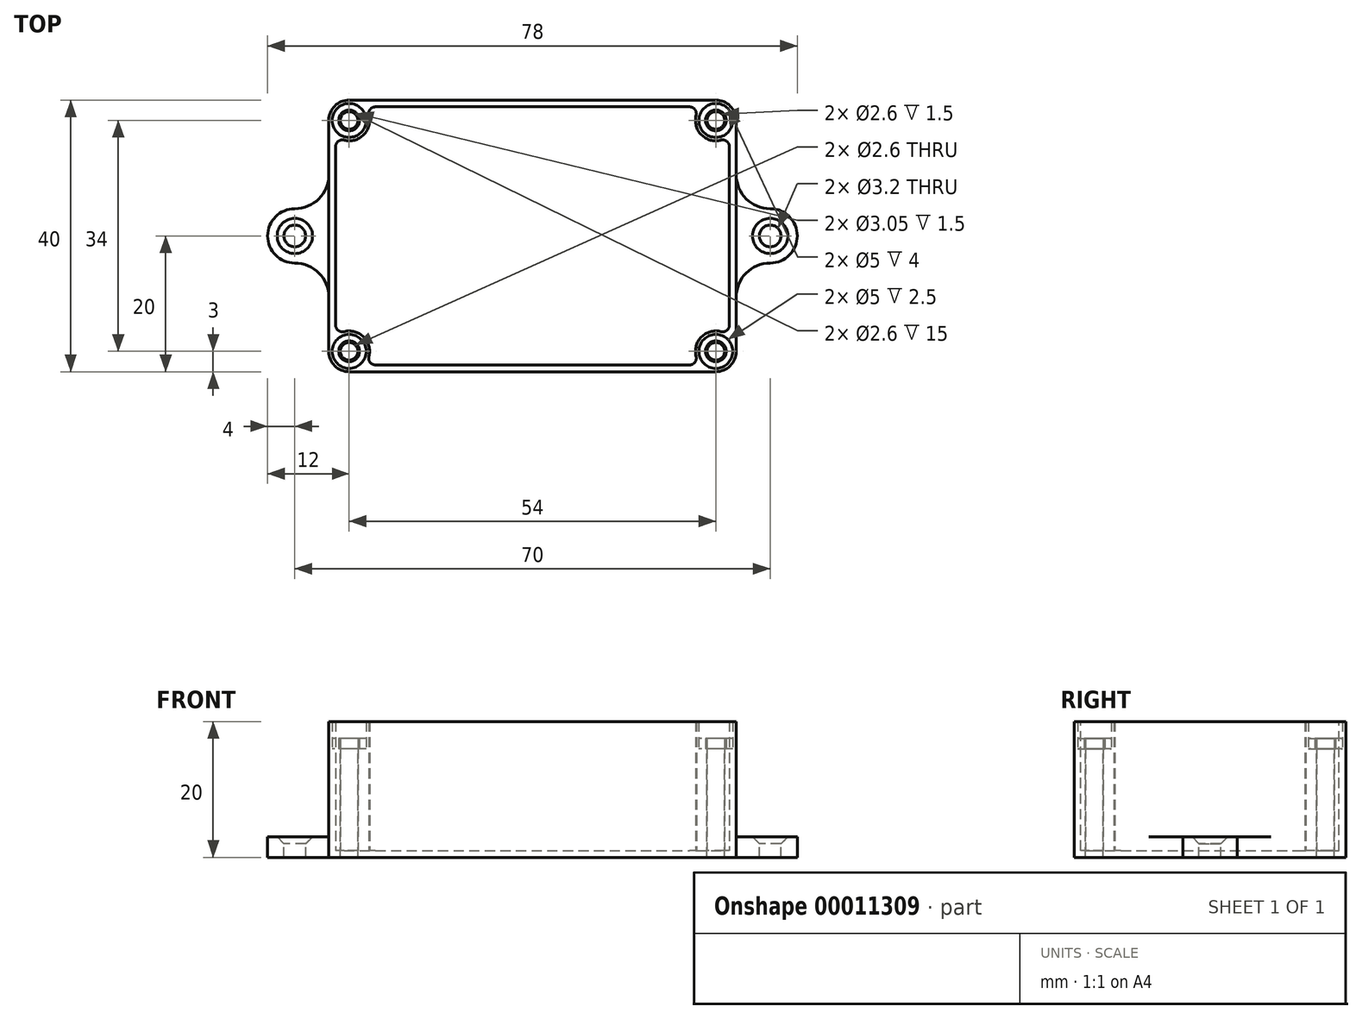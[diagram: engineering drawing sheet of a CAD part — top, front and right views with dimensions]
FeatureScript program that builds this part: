
annotation { "Feature Type Name" : "Feature", "Feature Type Description" : "" }
export const myFeature = defineFeature(function(context is Context, id is Id, definition is map)
    precondition{}
    {
        {
            var Q0;
            Q0=qCreatedBy(makeId("Top.planeOp"),FACE);
            var sketch = newSketch(context, id + "F0", { "sketchPlane" : qUnion([Q0])});
            skLineSegment(sketch, "E0.bottom", {"start": v(-27, 20) * mm, "end": v(27, 20) * mm});
            skLineSegment(sketch, "E0.top", {"start": v(-27, -20) * mm, "end": v(27, -20) * mm});
            skLineSegment(sketch, "E0.left", {"start": v(-30, 17) * mm, "end": v(-30, -17) * mm});
            skLineSegment(sketch, "E0.right", {"start": v(30, 17) * mm, "end": v(30, -17) * mm});
            skLineSegment(sketch, "E1", {"start": v(0, 0) * mm, "end": v(0, 30.82) * mm, "construction": true});
            skLineSegment(sketch, "E2", {"start": v(0, 0) * mm, "end": v(-60.1, 0) * mm, "construction": true});
            skArc(sketch, "E3", {"start": v(-27, 20) * mm, "mid": v(-29.12, 19.12) * mm, "end": v(-30, 17) * mm});
            skLineSegment(sketch, "E4", {"start": v(-30, -4) * mm, "end": v(-35, -4) * mm});
            skLineSegment(sketch, "E5", {"start": v(-30, 4) * mm, "end": v(-35, 4) * mm});
            skArc(sketch, "E6", {"start": v(-35, 4) * mm, "mid": v(-39, 0) * mm, "end": v(-35, -4) * mm});
            skCircle(sketch, "E7", {"center": v(-35, 0) * mm, "radius": 1.6 * mm});
            skLineSegment(sketch, "E8.0.MirrorCS", {"start": v(30, 4) * mm, "end": v(35, 4) * mm});
            skArc(sketch, "E9.0.MirrorCS", {"start": v(35, 4) * mm, "mid": v(39, 0) * mm, "end": v(35, -4) * mm});
            skCircle(sketch, "E10.0.MirrorC", {"center": v(35, 0) * mm, "radius": 1.6 * mm});
            skLineSegment(sketch, "E11.0.MirrorCS", {"start": v(30, -4) * mm, "end": v(35, -4) * mm});
            skCircle(sketch, "E12", {"center": v(-27, 17) * mm, "radius": 1.3 * mm});
            skLineSegment(sketch, "E13", {"start": v(-24.76, 19) * mm, "end": v(0, 19) * mm});
            skLineSegment(sketch, "E14", {"start": v(-29, 0) * mm, "end": v(-29, 14.76) * mm});
            skArc(sketch, "E15.trimOffspring", {"start": v(-29, 14.76) * mm, "mid": v(-24.88, 14.88) * mm, "end": v(-24.76, 19) * mm});
            skLineSegment(sketch, "E16.0.MirrorCS", {"start": v(24.76, 19) * mm, "end": v(0, 19) * mm});
            skArc(sketch, "E17.0.MirrorCS", {"start": v(29, 14.76) * mm, "mid": v(24.88, 14.88) * mm, "end": v(24.76, 19) * mm});
            skLineSegment(sketch, "E18.0.MirrorCS", {"start": v(29, 0) * mm, "end": v(29, 14.76) * mm});
            skCircle(sketch, "E19.0.MirrorC", {"center": v(27, 17) * mm, "radius": 1.3 * mm});
            skArc(sketch, "E20.0.MirrorCS", {"start": v(27, 20) * mm, "mid": v(29.12, 19.12) * mm, "end": v(30, 17) * mm});
            skLineSegment(sketch, "E21.0.MirrorCS", {"start": v(-29, 0) * mm, "end": v(-29, -14.76) * mm});
            skArc(sketch, "E22.0.MirrorCS", {"start": v(-29, -14.76) * mm, "mid": v(-24.88, -14.88) * mm, "end": v(-24.76, -19) * mm});
            skCircle(sketch, "E23.0.MirrorC", {"center": v(-27, -17) * mm, "radius": 1.3 * mm});
            skArc(sketch, "E24.0.MirrorCS", {"start": v(-27, -20) * mm, "mid": v(-29.12, -19.12) * mm, "end": v(-30, -17) * mm});
            skLineSegment(sketch, "E25.0.MirrorCS", {"start": v(-24.76, -19) * mm, "end": v(0, -19) * mm});
            skArc(sketch, "E26.0.MirrorCS", {"start": v(29, -14.76) * mm, "mid": v(24.88, -14.88) * mm, "end": v(24.76, -19) * mm});
            skCircle(sketch, "E27.0.MirrorC", {"center": v(27, -17) * mm, "radius": 1.3 * mm});
            skLineSegment(sketch, "E28.0.MirrorCS", {"start": v(24.76, -19) * mm, "end": v(0, -19) * mm});
            skLineSegment(sketch, "E29.0.MirrorCS", {"start": v(29, 0) * mm, "end": v(29, -14.76) * mm});
            skArc(sketch, "E30.0.MirrorCS", {"start": v(27, -20) * mm, "mid": v(29.12, -19.12) * mm, "end": v(30, -17) * mm});
            skSolve(sketch);
        }
        {
            var Q0;
            {var subQ1=sQuery(id+"F0.wireOp",EDGE,"E4");Q0=makeQuery(id+"F0.imprint","IMPRINT",FACE,{"disambiguationData":[TD([[makeQuery(id+"F0.imprint","IMPRINT",EDGE,{"derivedFrom":subQ1}),-1.0]])]});}
            var Q1;
            Q1=makeQuery(id+"F0.imprint","IMPRINT",FACE,{"disambiguationData":[TD([[makeQuery(id+"F0.imprint","IMPRINT",EDGE,{"derivedFrom":sQuery(id+"F0.wireOp",EDGE,"E0.bottom")}),-1.0]])]});
            var Q2;
            Q2=makeQuery(id+"F0.imprint","IMPRINT",FACE,{"disambiguationData":[TD([[makeQuery(id+"F0.imprint","IMPRINT",EDGE,{"derivedFrom":sQuery(id+"F0.wireOp",EDGE,"E12")}),1.0]])]});
            var Q3;
            Q3=makeQuery(id+"F0.imprint","IMPRINT",FACE,{"disambiguationData":[TD([[makeQuery(id+"F0.imprint","IMPRINT",EDGE,{"derivedFrom":sQuery(id+"F0.wireOp",EDGE,"E23.0.MirrorC")}),-1.0]])]});
            var Q4;
            Q4=makeQuery(id+"F0.imprint","IMPRINT",FACE,{"disambiguationData":[TD([[makeQuery(id+"F0.imprint","IMPRINT",EDGE,{"derivedFrom":sQuery(id+"F0.wireOp",EDGE,"E13")}),-1.0]])]});
            var Q5;
            Q5=makeQuery(id+"F0.imprint","IMPRINT",FACE,{"disambiguationData":[TD([[makeQuery(id+"F0.imprint","IMPRINT",EDGE,{"derivedFrom":sQuery(id+"F0.wireOp",EDGE,"E19.0.MirrorC")}),-1.0]])]});
            var Q6;
            Q6=makeQuery(id+"F0.imprint","IMPRINT",FACE,{"disambiguationData":[TD([[makeQuery(id+"F0.imprint","IMPRINT",EDGE,{"derivedFrom":sQuery(id+"F0.wireOp",EDGE,"E27.0.MirrorC")}),1.0]])]});
            var Q7;
            {var subQ1=sQuery(id+"F0.wireOp",EDGE,"E8.0.MirrorCS");Q7=makeQuery(id+"F0.imprint","IMPRINT",FACE,{"disambiguationData":[TD([[makeQuery(id+"F0.imprint","IMPRINT",EDGE,{"derivedFrom":subQ1}),-1.0]])]});}
            extrude(context, id + "F1", {"entities" : qUnion([Q0, Q1, Q2, Q3, Q4, Q5, Q6, Q7]), "oppositeDirection" : true, "depth" : 1 * mm});
        }
        {
            var Q0;
            Q0=makeQuery(id+"F1.opExtrude","SWEPT_EDGE",EDGE,{"disambiguationData":[OSD([sQuery(id+"F0.wireOp",EDGE,"E0.left"),sQuery(id+"F0.wireOp",EDGE,"E5")])]});
            var Q1;
            Q1=makeQuery(id+"F1.opExtrude","SWEPT_EDGE",EDGE,{"disambiguationData":[OSD([sQuery(id+"F0.wireOp",EDGE,"E0.left"),sQuery(id+"F0.wireOp",EDGE,"E4")])]});
            var Q2;
            Q2=makeQuery(id+"F1.opExtrude","SWEPT_EDGE",EDGE,{"disambiguationData":[OSD([sQuery(id+"F0.wireOp",EDGE,"E0.right"),sQuery(id+"F0.wireOp",EDGE,"E11.0.MirrorCS")])]});
            var Q3;
            Q3=makeQuery(id+"F1.opExtrude","SWEPT_EDGE",EDGE,{"disambiguationData":[OSD([sQuery(id+"F0.wireOp",EDGE,"E0.right"),sQuery(id+"F0.wireOp",EDGE,"E8.0.MirrorCS")])]});
            fillet(context, id + "F2", {"entities" : qUnion([Q0, Q1, Q2, Q3]), "radius" : 5 * mm, "tangentPropagation" : true, "allowEdgeOverflow" : false});
        }
        {
            var Q0;
            Q0=makeQuery(id+"F0.imprint","IMPRINT",FACE,{"disambiguationData":[TD([[makeQuery(id+"F0.imprint","IMPRINT",EDGE,{"derivedFrom":sQuery(id+"F0.wireOp",EDGE,"E0.bottom")}),-1.0]])]});
            extrude(context, id + "F3", {"entities" : qUnion([Q0]), "operationType" : NewBodyOperationType.ADD, "depth" : 15 * mm});
        }
        {
            var Q0;
            {var subQ0=sQuery(id+"F0.wireOp",EDGE,"E0.left");var subQ1=sQuery(id+"F0.wireOp",EDGE,"E3");var subQ2=sQuery(id+"F0.wireOp",EDGE,"E4");var subQ3=sQuery(id+"F0.wireOp",EDGE,"E5");var subQ4=sQuery(id+"F0.wireOp",EDGE,"E6");var subQ5=sQuery(id+"F0.wireOp",EDGE,"E7");var subQ6=sQuery(id+"F0.wireOp",EDGE,"E24.0.MirrorCS");Q0=makeQuery(id+"F3.boolean.opBoolean","SPLIT",FACE,{"disambiguationData":[TD([makeQuery(id+"F1.opExtrude","SWEPT_FACE",FACE,{"disambiguationData":[OSD([subQ4])]})])],"derivedFrom":makeQuery(id+"F1.opExtrude","CAP_FACE",FACE,{"disambiguationData":[OSD([sQuery(id+"F0.wireOp",EDGE,"E0.bottom"),sQuery(id+"F0.wireOp",EDGE,"E0.top"),subQ0,sQuery(id+"F0.wireOp",EDGE,"E0.right"),subQ1,subQ2,subQ3,subQ4,subQ5,sQuery(id+"F0.wireOp",EDGE,"E8.0.MirrorCS"),sQuery(id+"F0.wireOp",EDGE,"E9.0.MirrorCS"),sQuery(id+"F0.wireOp",EDGE,"E10.0.MirrorC"),sQuery(id+"F0.wireOp",EDGE,"E11.0.MirrorCS"),sQuery(id+"F0.wireOp",EDGE,"E20.0.MirrorCS"),subQ6,sQuery(id+"F0.wireOp",EDGE,"E30.0.MirrorCS")])],"isStart":true})});}
            var Q1;
            {var subQ0=sQuery(id+"F0.wireOp",EDGE,"E0.right");var subQ1=sQuery(id+"F0.wireOp",EDGE,"E8.0.MirrorCS");var subQ2=sQuery(id+"F0.wireOp",EDGE,"E9.0.MirrorCS");var subQ3=sQuery(id+"F0.wireOp",EDGE,"E10.0.MirrorC");var subQ4=sQuery(id+"F0.wireOp",EDGE,"E11.0.MirrorCS");var subQ5=sQuery(id+"F0.wireOp",EDGE,"E20.0.MirrorCS");var subQ6=sQuery(id+"F0.wireOp",EDGE,"E30.0.MirrorCS");Q1=makeQuery(id+"F3.boolean.opBoolean","SPLIT",FACE,{"disambiguationData":[TD([makeQuery(id+"F1.opExtrude","SWEPT_FACE",FACE,{"disambiguationData":[OSD([subQ2])]})])],"derivedFrom":makeQuery(id+"F1.opExtrude","CAP_FACE",FACE,{"disambiguationData":[OSD([sQuery(id+"F0.wireOp",EDGE,"E0.bottom"),sQuery(id+"F0.wireOp",EDGE,"E0.top"),sQuery(id+"F0.wireOp",EDGE,"E0.left"),subQ0,sQuery(id+"F0.wireOp",EDGE,"E3"),sQuery(id+"F0.wireOp",EDGE,"E4"),sQuery(id+"F0.wireOp",EDGE,"E5"),sQuery(id+"F0.wireOp",EDGE,"E6"),sQuery(id+"F0.wireOp",EDGE,"E7"),subQ1,subQ2,subQ3,subQ4,subQ5,sQuery(id+"F0.wireOp",EDGE,"E24.0.MirrorCS"),subQ6])],"isStart":true})});}
            extrude(context, id + "F4", {"entities" : qUnion([Q0, Q1]), "operationType" : NewBodyOperationType.ADD, "depth" : 2 * mm});
        }
        {
            var Q0;
            Q0=makeQuery(id+"F4.opExtrude","CAP_EDGE",EDGE,{"disambiguationData":[OSD([sQuery(id+"F0.wireOp",EDGE,"E7")])],"isStart":false});
            var Q1;
            Q1=makeQuery(id+"F4.opExtrude","CAP_EDGE",EDGE,{"disambiguationData":[OSD([sQuery(id+"F0.wireOp",EDGE,"E10.0.MirrorC")])],"isStart":false});
            chamfer(context, id + "F5", {"entities" : qUnion([Q0, Q1]), "width" : 1 * mm, "tangentPropagation" : true});
        }
        {
            var Q0;
            Q0=makeQuery(id+"F3.opExtrude","CAP_FACE",FACE,{"disambiguationData":[OSD([sQuery(id+"F0.wireOp",EDGE,"E0.bottom"),sQuery(id+"F0.wireOp",EDGE,"E0.top"),sQuery(id+"F0.wireOp",EDGE,"E0.left"),sQuery(id+"F0.wireOp",EDGE,"E0.right"),sQuery(id+"F0.wireOp",EDGE,"E3"),sQuery(id+"F0.wireOp",EDGE,"E12"),sQuery(id+"F0.wireOp",EDGE,"E13"),sQuery(id+"F0.wireOp",EDGE,"E14"),sQuery(id+"F0.wireOp",EDGE,"E15.trimOffspring"),sQuery(id+"F0.wireOp",EDGE,"E16.0.MirrorCS"),sQuery(id+"F0.wireOp",EDGE,"E17.0.MirrorCS"),sQuery(id+"F0.wireOp",EDGE,"E18.0.MirrorCS"),sQuery(id+"F0.wireOp",EDGE,"E19.0.MirrorC"),sQuery(id+"F0.wireOp",EDGE,"E20.0.MirrorCS"),sQuery(id+"F0.wireOp",EDGE,"E21.0.MirrorCS"),sQuery(id+"F0.wireOp",EDGE,"E22.0.MirrorCS"),sQuery(id+"F0.wireOp",EDGE,"E23.0.MirrorC"),sQuery(id+"F0.wireOp",EDGE,"E24.0.MirrorCS"),sQuery(id+"F0.wireOp",EDGE,"E25.0.MirrorCS"),sQuery(id+"F0.wireOp",EDGE,"E26.0.MirrorCS"),sQuery(id+"F0.wireOp",EDGE,"E27.0.MirrorC"),sQuery(id+"F0.wireOp",EDGE,"E28.0.MirrorCS"),sQuery(id+"F0.wireOp",EDGE,"E29.0.MirrorCS"),sQuery(id+"F0.wireOp",EDGE,"E30.0.MirrorCS")])],"isStart":false});
            var sketch = newSketch(context, id + "F6", { "sketchPlane" : qUnion([Q0])});
            skLineSegment(sketch, "E31.1", {"start": v(-27, 20) * mm, "end": v(27, 20) * mm});
            skArc(sketch, "E31.2", {"start": v(-27, 20) * mm, "mid": v(-29.12, 19.12) * mm, "end": v(-30, 17) * mm});
            skLineSegment(sketch, "E31.3", {"start": v(-30, 17) * mm, "end": v(-30, -17) * mm});
            skArc(sketch, "E31.4", {"start": v(-27, -20) * mm, "mid": v(-29.12, -19.12) * mm, "end": v(-30, -17) * mm});
            skLineSegment(sketch, "E31.5", {"start": v(-27, -20) * mm, "end": v(27, -20) * mm});
            skArc(sketch, "E31.6", {"start": v(27, -20) * mm, "mid": v(29.12, -19.12) * mm, "end": v(30, -17) * mm});
            skLineSegment(sketch, "E31.7", {"start": v(30, 17) * mm, "end": v(30, -17) * mm});
            skArc(sketch, "E31.8", {"start": v(27, 20) * mm, "mid": v(29.12, 19.12) * mm, "end": v(30, 17) * mm});
            skCircle(sketch, "E31.9", {"center": v(27, 17) * mm, "radius": 1.3 * mm});
            skArc(sketch, "E31.10", {"start": v(29, 14.76) * mm, "mid": v(24.88, 14.88) * mm, "end": v(24.76, 19) * mm});
            skLineSegment(sketch, "E31.11", {"start": v(29, -14.76) * mm, "end": v(29, 14.76) * mm});
            skArc(sketch, "E31.12", {"start": v(29, -14.76) * mm, "mid": v(24.88, -14.88) * mm, "end": v(24.76, -19) * mm});
            skLineSegment(sketch, "E31.13", {"start": v(24.76, -19) * mm, "end": v(-24.76, -19) * mm});
            skCircle(sketch, "E31.14", {"center": v(27, -17) * mm, "radius": 1.3 * mm});
            skArc(sketch, "E31.15", {"start": v(-29, -14.76) * mm, "mid": v(-24.88, -14.88) * mm, "end": v(-24.76, -19) * mm});
            skCircle(sketch, "E31.16", {"center": v(-27, -17) * mm, "radius": 1.3 * mm});
            skLineSegment(sketch, "E31.17", {"start": v(-29, 14.76) * mm, "end": v(-29, -14.76) * mm});
            skArc(sketch, "E31.18", {"start": v(-29, 14.76) * mm, "mid": v(-24.88, 14.88) * mm, "end": v(-24.76, 19) * mm});
            skCircle(sketch, "E31.20", {"center": v(-27, 17) * mm, "radius": 1.3 * mm});
            skLineSegment(sketch, "E31.21", {"start": v(-24.76, 19) * mm, "end": v(24.76, 19) * mm});
            skLineSegment(sketch, "E32.0", {"start": v(0, 0) * mm, "end": v(0, 30.82) * mm, "construction": true});
            skLineSegment(sketch, "E32.1", {"start": v(0, 0) * mm, "end": v(-60.1, 0) * mm, "construction": true});
            skCircle(sketch, "E33", {"center": v(-27, 17) * mm, "radius": 2.5 * mm});
            skCircle(sketch, "E34", {"center": v(-27, 17) * mm, "radius": 1.52 * mm});
            skCircle(sketch, "E35.0.MirrorC", {"center": v(27, 17) * mm, "radius": 1.52 * mm});
            skCircle(sketch, "E36.0.MirrorC", {"center": v(27, 17) * mm, "radius": 2.5 * mm});
            skCircle(sketch, "E37.0.MirrorC", {"center": v(-27, -17) * mm, "radius": 1.52 * mm});
            skCircle(sketch, "E38.0.MirrorC", {"center": v(-27, -17) * mm, "radius": 2.5 * mm});
            skCircle(sketch, "E39.0.MirrorC", {"center": v(27, -17) * mm, "radius": 1.52 * mm});
            skCircle(sketch, "E40.0.MirrorC", {"center": v(27, -17) * mm, "radius": 2.5 * mm});
            skArc(sketch, "E41.0", {"start": v(-28, 13.13) * mm, "mid": v(-24.17, 14.17) * mm, "end": v(-23.13, 18) * mm});
            skLineSegment(sketch, "E41.1", {"start": v(-28, 13.13) * mm, "end": v(-28, -13.13) * mm});
            skArc(sketch, "E41.2", {"start": v(-28, -13.13) * mm, "mid": v(-24.17, -14.17) * mm, "end": v(-23.13, -18) * mm});
            skLineSegment(sketch, "E41.3", {"start": v(23.13, -18) * mm, "end": v(-23.13, -18) * mm});
            skArc(sketch, "E41.4", {"start": v(28, -13.13) * mm, "mid": v(24.17, -14.17) * mm, "end": v(23.13, -18) * mm});
            skLineSegment(sketch, "E41.5", {"start": v(-23.13, 18) * mm, "end": v(23.13, 18) * mm});
            skLineSegment(sketch, "E41.6", {"start": v(28, -13.13) * mm, "end": v(28, 13.13) * mm});
            skArc(sketch, "E41.7", {"start": v(28, 13.13) * mm, "mid": v(24.17, 14.17) * mm, "end": v(23.13, 18) * mm});
            skSolve(sketch);
        }
        {
            var Q0;
            Q0=makeQuery(id+"F6.imprint","IMPRINT",FACE,{"disambiguationData":[TD([[makeQuery(id+"F6.imprint","IMPRINT",EDGE,{"derivedFrom":sQuery(id+"F6.wireOp",EDGE,"E31.1")}),-1.0]])]});
            var Q1;
            Q1=makeQuery(id+"F6.imprint","IMPRINT",FACE,{"disambiguationData":[TD([[makeQuery(id+"F6.imprint","IMPRINT",EDGE,{"derivedFrom":sQuery(id+"F6.wireOp",EDGE,"E33")}),1.0]])]});
            var Q2;
            Q2=makeQuery(id+"F6.imprint","IMPRINT",FACE,{"disambiguationData":[TD([[makeQuery(id+"F6.imprint","IMPRINT",EDGE,{"derivedFrom":sQuery(id+"F6.wireOp",EDGE,"E35.0.MirrorC")}),1.0]])]});
            var Q3;
            Q3=makeQuery(id+"F6.imprint","IMPRINT",FACE,{"disambiguationData":[TD([[makeQuery(id+"F6.imprint","IMPRINT",EDGE,{"derivedFrom":sQuery(id+"F6.wireOp",EDGE,"E39.0.MirrorC")}),-1.0]])]});
            var Q4;
            Q4=makeQuery(id+"F6.imprint","IMPRINT",FACE,{"disambiguationData":[TD([[makeQuery(id+"F6.imprint","IMPRINT",EDGE,{"derivedFrom":sQuery(id+"F6.wireOp",EDGE,"E37.0.MirrorC")}),1.0]])]});
            var Q5;
            Q5=makeQuery(id+"F6.imprint","IMPRINT",FACE,{"disambiguationData":[TD([[makeQuery(id+"F6.imprint","IMPRINT",EDGE,{"derivedFrom":sQuery(id+"F6.wireOp",EDGE,"E31.10")}),1.0]])]});
            extrude(context, id + "F7", {"entities" : qUnion([Q0, Q1, Q2, Q3, Q4, Q5]), "depth" : 3 * mm});
        }
        {
            var Q0;
            Q0=makeQuery(id+"F7.opExtrude","CAP_FACE",FACE,{"disambiguationData":[OSD([sQuery(id+"F6.wireOp",EDGE,"E31.1"),sQuery(id+"F6.wireOp",EDGE,"E31.2"),sQuery(id+"F6.wireOp",EDGE,"E31.3"),sQuery(id+"F6.wireOp",EDGE,"E31.4"),sQuery(id+"F6.wireOp",EDGE,"E31.5"),sQuery(id+"F6.wireOp",EDGE,"E31.6"),sQuery(id+"F6.wireOp",EDGE,"E31.7"),sQuery(id+"F6.wireOp",EDGE,"E31.8"),sQuery(id+"F6.wireOp",EDGE,"E31.10"),sQuery(id+"F6.wireOp",EDGE,"E31.11"),sQuery(id+"F6.wireOp",EDGE,"E31.12"),sQuery(id+"F6.wireOp",EDGE,"E31.13"),sQuery(id+"F6.wireOp",EDGE,"E31.15"),sQuery(id+"F6.wireOp",EDGE,"E31.17"),sQuery(id+"F6.wireOp",EDGE,"E31.18"),sQuery(id+"F6.wireOp",EDGE,"E31.21"),sQuery(id+"F6.wireOp",EDGE,"E34"),sQuery(id+"F6.wireOp",EDGE,"E35.0.MirrorC"),sQuery(id+"F6.wireOp",EDGE,"E37.0.MirrorC"),sQuery(id+"F6.wireOp",EDGE,"E39.0.MirrorC")])],"isStart":false});
            var sketch = newSketch(context, id + "F8", { "sketchPlane" : qUnion([Q0])});
            skLineSegment(sketch, "E42.0", {"start": v(-27, 20) * mm, "end": v(27, 20) * mm});
            skArc(sketch, "E42.1", {"start": v(-27, 20) * mm, "mid": v(-29.12, 19.12) * mm, "end": v(-30, 17) * mm});
            skLineSegment(sketch, "E42.2", {"start": v(-30, 17) * mm, "end": v(-30, -17) * mm});
            skArc(sketch, "E42.3", {"start": v(-27, -20) * mm, "mid": v(-29.12, -19.12) * mm, "end": v(-30, -17) * mm});
            skCircle(sketch, "E42.4", {"center": v(-27, -17) * mm, "radius": 1.52 * mm});
            skLineSegment(sketch, "E42.5", {"start": v(-27, -20) * mm, "end": v(27, -20) * mm});
            skArc(sketch, "E42.6", {"start": v(27, -20) * mm, "mid": v(29.12, -19.12) * mm, "end": v(30, -17) * mm});
            skCircle(sketch, "E42.7", {"center": v(27, -17) * mm, "radius": 1.52 * mm});
            skLineSegment(sketch, "E42.8", {"start": v(30, 17) * mm, "end": v(30, -17) * mm});
            skArc(sketch, "E42.9", {"start": v(27, 20) * mm, "mid": v(29.12, 19.12) * mm, "end": v(30, 17) * mm});
            skCircle(sketch, "E42.10", {"center": v(27, 17) * mm, "radius": 1.52 * mm});
            skCircle(sketch, "E42.11", {"center": v(-27, 17) * mm, "radius": 1.52 * mm});
            skCircle(sketch, "E43", {"center": v(-27, 17) * mm, "radius": 2.5 * mm});
            skCircle(sketch, "E44.0.MirrorC", {"center": v(27, 17) * mm, "radius": 2.5 * mm});
            skCircle(sketch, "E45.0.MirrorC", {"center": v(27, -17) * mm, "radius": 2.5 * mm});
            skCircle(sketch, "E46.0.MirrorC", {"center": v(-27, -17) * mm, "radius": 2.5 * mm});
            skSolve(sketch);
        }
        {
            var Q0;
            Q0=makeQuery(id+"F8.imprint","IMPRINT",FACE,{"disambiguationData":[TD([[makeQuery(id+"F8.imprint","IMPRINT",EDGE,{"derivedFrom":sQuery(id+"F8.wireOp",EDGE,"E42.0")}),-1.0]])]});
            var Q1;
            Q1=makeQuery(id+"F8.imprint","IMPRINT",FACE,{"disambiguationData":[TD([[makeQuery(id+"F8.imprint","IMPRINT",EDGE,{"derivedFrom":makeQuery(id+"F7.opExtrude","CAP_EDGE",EDGE,{"disambiguationData":[OSD([sQuery(id+"F6.wireOp",EDGE,"E31.10")])],"isStart":false})}),1.0]])]});
            var Q2;
            Q2=makeQuery(id+"F8.imprint","IMPRINT",FACE,{"disambiguationData":[TD([[makeQuery(id+"F8.imprint","IMPRINT",EDGE,{"derivedFrom":makeQuery(id+"F7.opExtrude","CAP_EDGE",EDGE,{"disambiguationData":[OSD([sQuery(id+"F6.wireOp",EDGE,"E41.0")])],"isStart":false})}),-1.0]])]});
            extrude(context, id + "F9", {"entities" : qUnion([Q0, Q1, Q2]), "operationType" : NewBodyOperationType.ADD, "depth" : 1 * mm});
        }
        {
            var Q0;
            Q0=makeQuery(id+"F8.imprint","IMPRINT",FACE,{"disambiguationData":[TD([[makeQuery(id+"F8.imprint","IMPRINT",EDGE,{"derivedFrom":sQuery(id+"F8.wireOp",EDGE,"E42.11")}),-1.0]])]});
            var Q1;
            Q1=makeQuery(id+"F8.imprint","IMPRINT",FACE,{"disambiguationData":[TD([[makeQuery(id+"F8.imprint","IMPRINT",EDGE,{"derivedFrom":sQuery(id+"F8.wireOp",EDGE,"E42.10")}),1.0]])]});
            var Q2;
            Q2=makeQuery(id+"F8.imprint","IMPRINT",FACE,{"disambiguationData":[TD([[makeQuery(id+"F8.imprint","IMPRINT",EDGE,{"derivedFrom":sQuery(id+"F8.wireOp",EDGE,"E42.7")}),-1.0]])]});
            var Q3;
            Q3=makeQuery(id+"F8.imprint","IMPRINT",FACE,{"disambiguationData":[TD([[makeQuery(id+"F8.imprint","IMPRINT",EDGE,{"derivedFrom":sQuery(id+"F8.wireOp",EDGE,"E42.4")}),1.0]])]});
            extrude(context, id + "F10", {"entities" : qUnion([Q0, Q1, Q2, Q3]), "operationType" : NewBodyOperationType.REMOVE, "oppositeDirection" : true, "depth" : 1.5 * mm});
        }
        {
            var Q0;
            Q0=makeQuery(id+"F6.imprint","IMPRINT",FACE,{"disambiguationData":[TD([[makeQuery(id+"F6.imprint","IMPRINT",EDGE,{"derivedFrom":sQuery(id+"F6.wireOp",EDGE,"E31.10")}),1.0]])]});
            extrude(context, id + "F11", {"entities" : qUnion([Q0]), "operationType" : NewBodyOperationType.ADD, "oppositeDirection" : true, "depth" : 1 * mm});
        }
        {
            var Q0;
            Q0=makeQuery(id+"F11.opExtrude","SWEPT_EDGE",EDGE,{"disambiguationData":[OSD([sQuery(id+"F6.wireOp",EDGE,"E31.15"),sQuery(id+"F6.wireOp",EDGE,"E31.17")])]});
            var Q1;
            Q1=makeQuery(id+"F11.opExtrude","SWEPT_EDGE",EDGE,{"disambiguationData":[OSD([sQuery(id+"F6.wireOp",EDGE,"E31.13"),sQuery(id+"F6.wireOp",EDGE,"E31.15")])]});
            var Q2;
            {var subQ0=sQuery(id+"F6.wireOp",EDGE,"E41.2");var subQ1=sQuery(id+"F6.wireOp",EDGE,"E41.3");Q2=makeQuery(id+"F11.boolean.opBoolean","MERGE",EDGE,{"derivedFrom":[makeQuery(id+"F7.opExtrude","SWEPT_EDGE",EDGE,{"disambiguationData":[OSD([subQ0,subQ1])]}),makeQuery(id+"F11.opExtrude","SWEPT_EDGE",EDGE,{"disambiguationData":[OSD([subQ0,subQ1])]})]});}
            var Q3;
            {var subQ0=sQuery(id+"F6.wireOp",EDGE,"E41.1");var subQ1=sQuery(id+"F6.wireOp",EDGE,"E41.2");Q3=makeQuery(id+"F11.boolean.opBoolean","MERGE",EDGE,{"derivedFrom":[makeQuery(id+"F7.opExtrude","SWEPT_EDGE",EDGE,{"disambiguationData":[OSD([subQ0,subQ1])]}),makeQuery(id+"F11.opExtrude","SWEPT_EDGE",EDGE,{"disambiguationData":[OSD([subQ0,subQ1])]})]});}
            var Q4;
            Q4=makeQuery(id+"F11.opExtrude","SWEPT_EDGE",EDGE,{"disambiguationData":[OSD([sQuery(id+"F6.wireOp",EDGE,"E31.17"),sQuery(id+"F6.wireOp",EDGE,"E31.18")])]});
            var Q5;
            Q5=makeQuery(id+"F11.opExtrude","SWEPT_EDGE",EDGE,{"disambiguationData":[OSD([sQuery(id+"F6.wireOp",EDGE,"E31.18"),sQuery(id+"F6.wireOp",EDGE,"E31.21")])]});
            var Q6;
            {var subQ0=sQuery(id+"F6.wireOp",EDGE,"E41.0");var subQ1=sQuery(id+"F6.wireOp",EDGE,"E41.1");Q6=makeQuery(id+"F11.boolean.opBoolean","MERGE",EDGE,{"derivedFrom":[makeQuery(id+"F7.opExtrude","SWEPT_EDGE",EDGE,{"disambiguationData":[OSD([subQ0,subQ1])]}),makeQuery(id+"F11.opExtrude","SWEPT_EDGE",EDGE,{"disambiguationData":[OSD([subQ0,subQ1])]})]});}
            var Q7;
            {var subQ0=sQuery(id+"F6.wireOp",EDGE,"E41.0");var subQ1=sQuery(id+"F6.wireOp",EDGE,"E41.5");Q7=makeQuery(id+"F11.boolean.opBoolean","MERGE",EDGE,{"derivedFrom":[makeQuery(id+"F7.opExtrude","SWEPT_EDGE",EDGE,{"disambiguationData":[OSD([subQ0,subQ1])]}),makeQuery(id+"F11.opExtrude","SWEPT_EDGE",EDGE,{"disambiguationData":[OSD([subQ0,subQ1])]})]});}
            var Q8;
            {var subQ0=sQuery(id+"F6.wireOp",EDGE,"E41.3");var subQ1=sQuery(id+"F6.wireOp",EDGE,"E41.4");Q8=makeQuery(id+"F11.boolean.opBoolean","MERGE",EDGE,{"derivedFrom":[makeQuery(id+"F7.opExtrude","SWEPT_EDGE",EDGE,{"disambiguationData":[OSD([subQ0,subQ1])]}),makeQuery(id+"F11.opExtrude","SWEPT_EDGE",EDGE,{"disambiguationData":[OSD([subQ0,subQ1])]})]});}
            var Q9;
            {var subQ0=sQuery(id+"F6.wireOp",EDGE,"E41.4");var subQ1=sQuery(id+"F6.wireOp",EDGE,"E41.6");Q9=makeQuery(id+"F11.boolean.opBoolean","MERGE",EDGE,{"derivedFrom":[makeQuery(id+"F7.opExtrude","SWEPT_EDGE",EDGE,{"disambiguationData":[OSD([subQ0,subQ1])]}),makeQuery(id+"F11.opExtrude","SWEPT_EDGE",EDGE,{"disambiguationData":[OSD([subQ0,subQ1])]})]});}
            var Q10;
            Q10=makeQuery(id+"F11.opExtrude","SWEPT_EDGE",EDGE,{"disambiguationData":[OSD([sQuery(id+"F6.wireOp",EDGE,"E31.12"),sQuery(id+"F6.wireOp",EDGE,"E31.13")])]});
            var Q11;
            Q11=makeQuery(id+"F11.opExtrude","SWEPT_EDGE",EDGE,{"disambiguationData":[OSD([sQuery(id+"F6.wireOp",EDGE,"E31.11"),sQuery(id+"F6.wireOp",EDGE,"E31.12")])]});
            var Q12;
            Q12=makeQuery(id+"F11.opExtrude","SWEPT_EDGE",EDGE,{"disambiguationData":[OSD([sQuery(id+"F6.wireOp",EDGE,"E31.10"),sQuery(id+"F6.wireOp",EDGE,"E31.21")])]});
            var Q13;
            Q13=makeQuery(id+"F11.opExtrude","SWEPT_EDGE",EDGE,{"disambiguationData":[OSD([sQuery(id+"F6.wireOp",EDGE,"E31.10"),sQuery(id+"F6.wireOp",EDGE,"E31.11")])]});
            var Q14;
            {var subQ0=sQuery(id+"F6.wireOp",EDGE,"E41.6");var subQ1=sQuery(id+"F6.wireOp",EDGE,"E41.7");Q14=makeQuery(id+"F11.boolean.opBoolean","MERGE",EDGE,{"derivedFrom":[makeQuery(id+"F7.opExtrude","SWEPT_EDGE",EDGE,{"disambiguationData":[OSD([subQ0,subQ1])]}),makeQuery(id+"F11.opExtrude","SWEPT_EDGE",EDGE,{"disambiguationData":[OSD([subQ0,subQ1])]})]});}
            var Q15;
            {var subQ0=sQuery(id+"F6.wireOp",EDGE,"E41.5");var subQ1=sQuery(id+"F6.wireOp",EDGE,"E41.7");Q15=makeQuery(id+"F11.boolean.opBoolean","MERGE",EDGE,{"derivedFrom":[makeQuery(id+"F7.opExtrude","SWEPT_EDGE",EDGE,{"disambiguationData":[OSD([subQ0,subQ1])]}),makeQuery(id+"F11.opExtrude","SWEPT_EDGE",EDGE,{"disambiguationData":[OSD([subQ0,subQ1])]})]});}
            fillet(context, id + "F12", {"entities" : qUnion([Q0, Q1, Q2, Q3, Q4, Q5, Q6, Q7, Q8, Q9, Q10, Q11, Q12, Q13, Q14, Q15]), "radius" : 1 * mm, "tangentPropagation" : true, "allowEdgeOverflow" : false});
        }
    });
